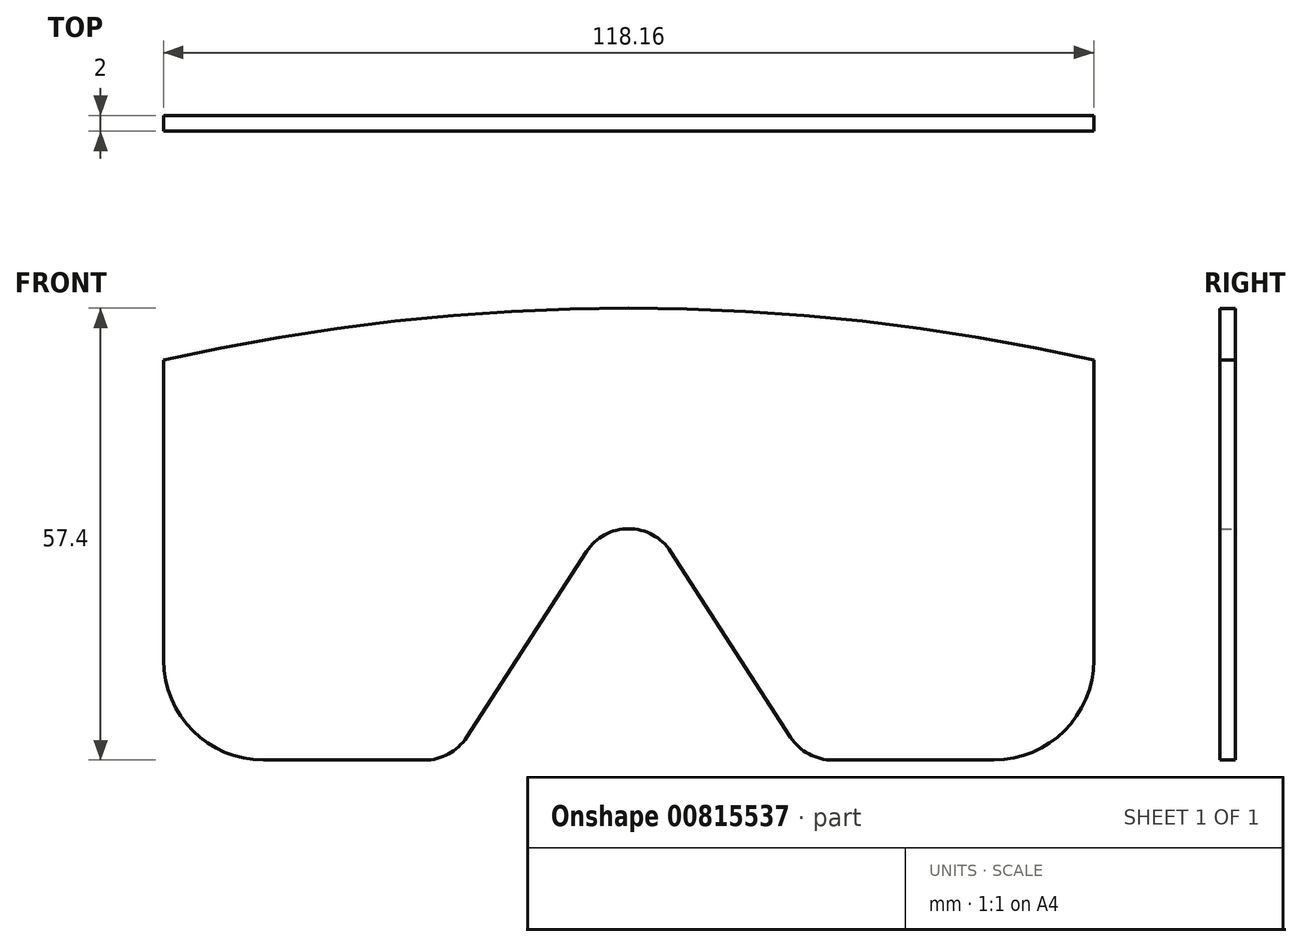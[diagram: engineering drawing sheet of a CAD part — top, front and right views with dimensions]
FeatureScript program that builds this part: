
annotation { "Feature Type Name" : "Feature", "Feature Type Description" : "" }
export const myFeature = defineFeature(function(context is Context, id is Id, definition is map)
    precondition{}
    {
        {
            var Q0;
            Q0=qCreatedBy(makeId("Front.planeOp"),FACE);
            var sketch = newSketch(context, id + "F0", { "sketchPlane" : qUnion([Q0])});
            skLineSegment(sketch, "E0", {"start": v(5.33, -8.25) * mm, "end": v(20.58, -31.83) * mm});
            skLineSegment(sketch, "E1", {"start": v(25.91, -34.74) * mm, "end": v(46.38, -34.74) * mm});
            skLineSegment(sketch, "E2", {"start": v(59.08, -22.04) * mm, "end": v(59.08, 16.06) * mm});
            skLineSegment(sketch, "E3", {"start": v(-59.08, 16.06) * mm, "end": v(-59.08, -22.04) * mm});
            skLineSegment(sketch, "E4", {"start": v(-46.38, -34.74) * mm, "end": v(-25.91, -34.74) * mm});
            skLineSegment(sketch, "E5", {"start": v(-20.58, -31.83) * mm, "end": v(-5.33, -8.25) * mm});
            skPoint(sketch, "E6.visualSharp", {"position": v(0, 0) * mm});
            skArc(sketch, "E6.filletArc", {"start": v(5.33, -8.25) * mm, "mid": v(0, -5.35) * mm, "end": v(-5.33, -8.25) * mm});
            skLineSegment(sketch, "E7", {"start": v(0, 0) * mm, "end": v(0, 65) * mm, "construction": true});
            skPoint(sketch, "E8.visualSharp", {"position": v(-22.46, -34.74) * mm});
            skArc(sketch, "E8.filletArc", {"start": v(-25.91, -34.74) * mm, "mid": v(-22.88, -33.96) * mm, "end": v(-20.58, -31.83) * mm});
            skPoint(sketch, "E9.visualSharp", {"position": v(22.46, -34.74) * mm});
            skArc(sketch, "E9.filletArc", {"start": v(20.58, -31.83) * mm, "mid": v(22.88, -33.96) * mm, "end": v(25.91, -34.74) * mm});
            skPoint(sketch, "E10.visualSharp", {"position": v(-59.08, -34.74) * mm});
            skArc(sketch, "E10.filletArc", {"start": v(-59.08, -22.04) * mm, "mid": v(-55.36, -31.02) * mm, "end": v(-46.38, -34.74) * mm});
            skPoint(sketch, "E11.visualSharp", {"position": v(59.08, -34.74) * mm});
            skArc(sketch, "E11.filletArc", {"start": v(46.38, -34.74) * mm, "mid": v(55.36, -31.02) * mm, "end": v(59.08, -22.04) * mm});
            skArc(sketch, "E12", {"start": v(59.08, 16.06) * mm, "mid": v(0, 22.66) * mm, "end": v(-59.08, 16.06) * mm});
            skSolve(sketch);
        }
        {
            var Q0;
            Q0 = qSketchRegion(id + "F0", true);
            extrude(context, id + "F1", {"entities" : qUnion([Q0]), "depth" : 2 * mm, "offsetDistance" : 25.4 * mm});
        }
    });
